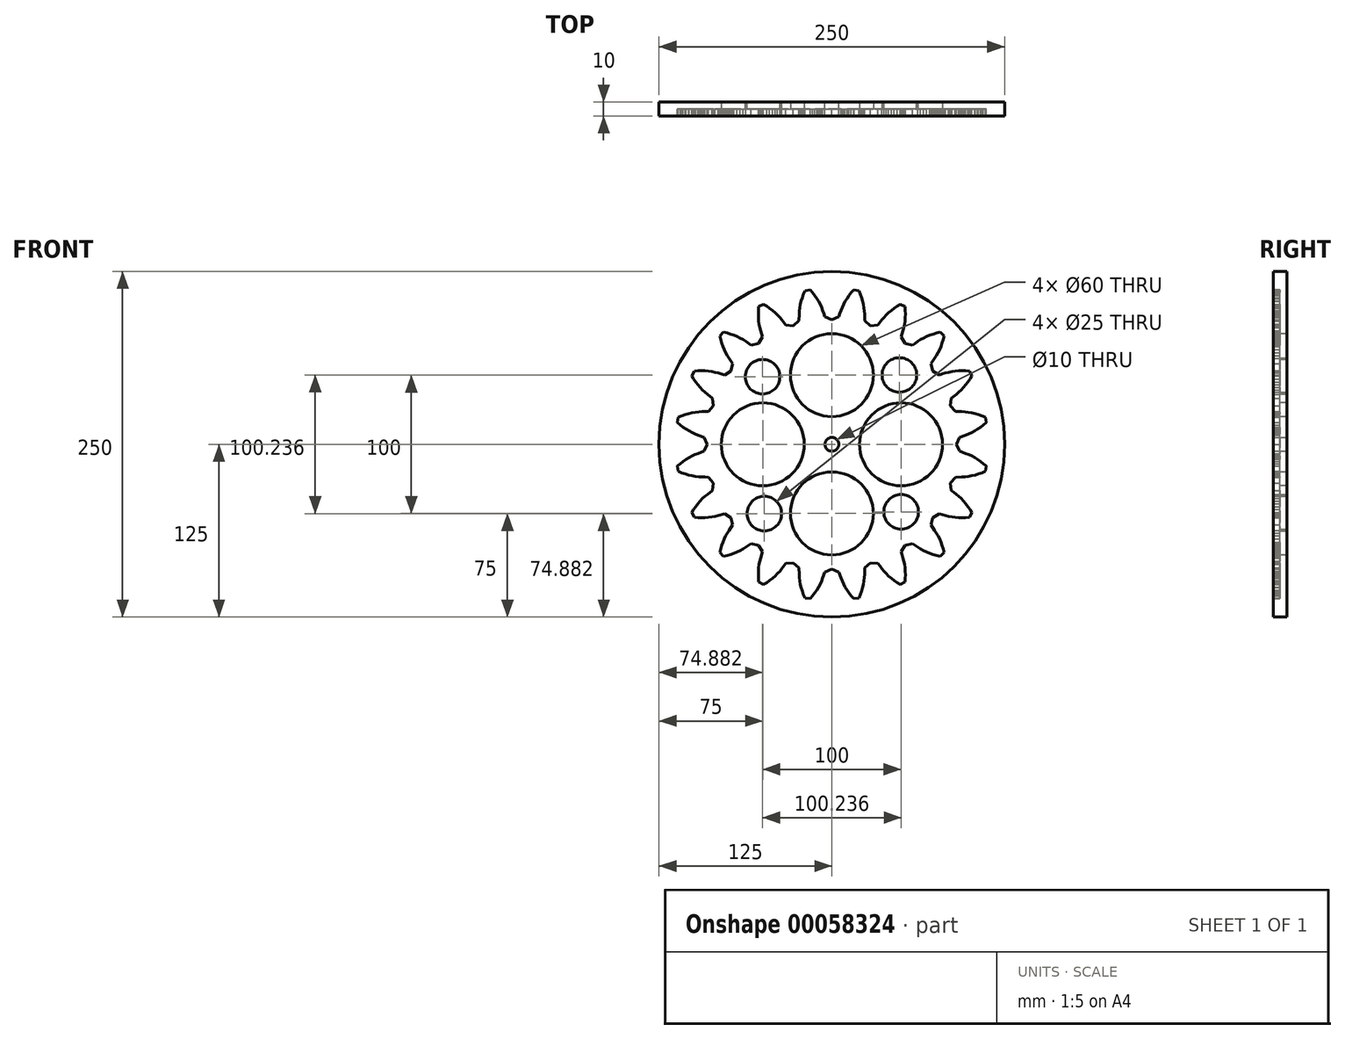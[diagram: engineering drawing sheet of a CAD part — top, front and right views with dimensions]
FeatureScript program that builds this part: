
annotation { "Feature Type Name" : "Feature", "Feature Type Description" : "" }
export const myFeature = defineFeature(function(context is Context, id is Id, definition is map)
    precondition{}
    {
        {
            var Q0;
            Q0=qCreatedBy(makeId("Front.planeOp"),FACE);
            var sketch = newSketch(context, id + "F0", { "sketchPlane" : qUnion([Q0])});
            skLineSegment(sketch, "E0", {"start": v(15.7, 111.67) * mm, "end": v(13.98, 109.62) * mm});
            skLineSegment(sketch, "E1", {"start": v(13.98, 109.62) * mm, "end": v(12.4, 107.54) * mm});
            skLineSegment(sketch, "E2", {"start": v(12.4, 107.54) * mm, "end": v(10.93, 105.44) * mm});
            skLineSegment(sketch, "E3", {"start": v(10.93, 105.44) * mm, "end": v(9.61, 103.3) * mm});
            skLineSegment(sketch, "E4", {"start": v(9.61, 103.3) * mm, "end": v(8.44, 101.14) * mm});
            skLineSegment(sketch, "E5", {"start": v(8.44, 101.14) * mm, "end": v(7.44, 98.96) * mm});
            skLineSegment(sketch, "E6", {"start": v(7.44, 98.96) * mm, "end": v(6.6, 96.75) * mm});
            skLineSegment(sketch, "E7", {"start": v(6.6, 96.75) * mm, "end": v(5.8, 94.55) * mm});
            skLineSegment(sketch, "E8", {"start": v(5.8, 94.55) * mm, "end": v(5, 92.33) * mm});
            skLineSegment(sketch, "E9", {"start": v(5, 92.33) * mm, "end": v(0, 90.21) * mm});
            skLineSegment(sketch, "E10", {"start": v(0, 90.21) * mm, "end": v(-5, 92.33) * mm});
            skLineSegment(sketch, "E11", {"start": v(-5, 92.33) * mm, "end": v(-5.8, 94.55) * mm});
            skLineSegment(sketch, "E12", {"start": v(-5.8, 94.55) * mm, "end": v(-6.6, 96.75) * mm});
            skLineSegment(sketch, "E13", {"start": v(-6.6, 96.75) * mm, "end": v(-7.44, 98.96) * mm});
            skLineSegment(sketch, "E14", {"start": v(-7.44, 98.96) * mm, "end": v(-8.44, 101.14) * mm});
            skLineSegment(sketch, "E15", {"start": v(-8.44, 101.14) * mm, "end": v(-9.61, 103.3) * mm});
            skLineSegment(sketch, "E16", {"start": v(-9.61, 103.3) * mm, "end": v(-10.93, 105.44) * mm});
            skLineSegment(sketch, "E17", {"start": v(-10.93, 105.44) * mm, "end": v(-12.4, 107.54) * mm});
            skLineSegment(sketch, "E18", {"start": v(-12.4, 107.54) * mm, "end": v(-13.98, 109.62) * mm});
            skLineSegment(sketch, "E19", {"start": v(-13.98, 109.62) * mm, "end": v(-15.7, 111.67) * mm});
            skLineSegment(sketch, "E20", {"start": v(-15.7, 111.67) * mm, "end": v(-19.57, 111.06) * mm});
            skLineSegment(sketch, "E21", {"start": v(-19.57, 111.06) * mm, "end": v(-20.58, 108.58) * mm});
            skLineSegment(sketch, "E22", {"start": v(-20.58, 108.58) * mm, "end": v(-21.45, 106.1) * mm});
            skLineSegment(sketch, "E23", {"start": v(-21.45, 106.1) * mm, "end": v(-22.18, 103.65) * mm});
            skLineSegment(sketch, "E24", {"start": v(-22.18, 103.65) * mm, "end": v(-22.78, 101.21) * mm});
            skLineSegment(sketch, "E25", {"start": v(-22.78, 101.21) * mm, "end": v(-23.22, 98.8) * mm});
            skLineSegment(sketch, "E26", {"start": v(-23.22, 98.8) * mm, "end": v(-23.5, 96.41) * mm});
            skLineSegment(sketch, "E27", {"start": v(-23.5, 96.41) * mm, "end": v(-23.62, 94.06) * mm});
            skLineSegment(sketch, "E28", {"start": v(-23.62, 94.06) * mm, "end": v(-23.7, 91.71) * mm});
            skLineSegment(sketch, "E29", {"start": v(-23.7, 91.71) * mm, "end": v(-23.78, 89.36) * mm});
            skLineSegment(sketch, "E30", {"start": v(-23.78, 89.36) * mm, "end": v(-27.88, 85.8) * mm});
            skLineSegment(sketch, "E31", {"start": v(-27.88, 85.8) * mm, "end": v(-33.28, 86.27) * mm});
            skLineSegment(sketch, "E32", {"start": v(-33.28, 86.27) * mm, "end": v(-34.73, 88.13) * mm});
            skLineSegment(sketch, "E33", {"start": v(-34.73, 88.13) * mm, "end": v(-36.18, 89.98) * mm});
            skLineSegment(sketch, "E34", {"start": v(-36.18, 89.98) * mm, "end": v(-37.65, 91.81) * mm});
            skLineSegment(sketch, "E35", {"start": v(-37.65, 91.81) * mm, "end": v(-39.28, 93.58) * mm});
            skLineSegment(sketch, "E36", {"start": v(-39.28, 93.58) * mm, "end": v(-41.06, 95.27) * mm});
            skLineSegment(sketch, "E37", {"start": v(-41.06, 95.27) * mm, "end": v(-42.98, 96.9) * mm});
            skLineSegment(sketch, "E38", {"start": v(-42.98, 96.9) * mm, "end": v(-45.02, 98.45) * mm});
            skLineSegment(sketch, "E39", {"start": v(-45.02, 98.45) * mm, "end": v(-47.18, 99.94) * mm});
            skLineSegment(sketch, "E40", {"start": v(-47.18, 99.94) * mm, "end": v(-49.44, 101.35) * mm});
            skLineSegment(sketch, "E41", {"start": v(-49.44, 101.35) * mm, "end": v(-52.93, 99.57) * mm});
            skLineSegment(sketch, "E42", {"start": v(-52.93, 99.57) * mm, "end": v(-53.12, 96.9) * mm});
            skLineSegment(sketch, "E43", {"start": v(-53.12, 96.9) * mm, "end": v(-53.19, 94.29) * mm});
            skLineSegment(sketch, "E44", {"start": v(-53.19, 94.29) * mm, "end": v(-53.13, 91.72) * mm});
            skLineSegment(sketch, "E45", {"start": v(-53.13, 91.72) * mm, "end": v(-52.94, 89.22) * mm});
            skLineSegment(sketch, "E46", {"start": v(-52.94, 89.22) * mm, "end": v(-52.62, 86.79) * mm});
            skLineSegment(sketch, "E47", {"start": v(-52.62, 86.79) * mm, "end": v(-52.15, 84.43) * mm});
            skLineSegment(sketch, "E48", {"start": v(-52.15, 84.43) * mm, "end": v(-51.53, 82.16) * mm});
            skLineSegment(sketch, "E49", {"start": v(-51.53, 82.16) * mm, "end": v(-50.88, 79.9) * mm});
            skLineSegment(sketch, "E50", {"start": v(-50.88, 79.9) * mm, "end": v(-50.23, 77.64) * mm});
            skLineSegment(sketch, "E51", {"start": v(-50.23, 77.64) * mm, "end": v(-53.03, 72.98) * mm});
            skLineSegment(sketch, "E52", {"start": v(-53.03, 72.98) * mm, "end": v(-58.31, 71.76) * mm});
            skLineSegment(sketch, "E53", {"start": v(-58.31, 71.76) * mm, "end": v(-60.27, 73.08) * mm});
            skLineSegment(sketch, "E54", {"start": v(-60.27, 73.08) * mm, "end": v(-62.21, 74.4) * mm});
            skLineSegment(sketch, "E55", {"start": v(-62.21, 74.4) * mm, "end": v(-64.18, 75.68) * mm});
            skLineSegment(sketch, "E56", {"start": v(-64.18, 75.68) * mm, "end": v(-66.28, 76.86) * mm});
            skLineSegment(sketch, "E57", {"start": v(-66.28, 76.86) * mm, "end": v(-68.5, 77.92) * mm});
            skLineSegment(sketch, "E58", {"start": v(-68.5, 77.92) * mm, "end": v(-70.82, 78.87) * mm});
            skLineSegment(sketch, "E59", {"start": v(-70.82, 78.87) * mm, "end": v(-73.24, 79.72) * mm});
            skLineSegment(sketch, "E60", {"start": v(-73.24, 79.72) * mm, "end": v(-75.75, 80.47) * mm});
            skLineSegment(sketch, "E61", {"start": v(-75.75, 80.47) * mm, "end": v(-78.34, 81.1) * mm});
            skLineSegment(sketch, "E62", {"start": v(-78.34, 81.1) * mm, "end": v(-81.1, 78.34) * mm});
            skLineSegment(sketch, "E63", {"start": v(-81.1, 78.34) * mm, "end": v(-80.47, 75.75) * mm});
            skLineSegment(sketch, "E64", {"start": v(-80.47, 75.75) * mm, "end": v(-79.72, 73.24) * mm});
            skLineSegment(sketch, "E65", {"start": v(-79.72, 73.24) * mm, "end": v(-78.87, 70.82) * mm});
            skLineSegment(sketch, "E66", {"start": v(-78.87, 70.82) * mm, "end": v(-77.92, 68.5) * mm});
            skLineSegment(sketch, "E67", {"start": v(-77.92, 68.5) * mm, "end": v(-76.86, 66.28) * mm});
            skLineSegment(sketch, "E68", {"start": v(-76.86, 66.28) * mm, "end": v(-75.68, 64.18) * mm});
            skLineSegment(sketch, "E69", {"start": v(-75.68, 64.18) * mm, "end": v(-74.4, 62.21) * mm});
            skLineSegment(sketch, "E70", {"start": v(-74.4, 62.21) * mm, "end": v(-73.08, 60.27) * mm});
            skLineSegment(sketch, "E71", {"start": v(-73.08, 60.27) * mm, "end": v(-71.76, 58.31) * mm});
            skLineSegment(sketch, "E72", {"start": v(-71.76, 58.31) * mm, "end": v(-72.98, 53.03) * mm});
            skLineSegment(sketch, "E73", {"start": v(-72.98, 53.03) * mm, "end": v(-77.64, 50.23) * mm});
            skLineSegment(sketch, "E74", {"start": v(-77.64, 50.23) * mm, "end": v(-79.9, 50.88) * mm});
            skLineSegment(sketch, "E75", {"start": v(-79.9, 50.88) * mm, "end": v(-82.16, 51.53) * mm});
            skLineSegment(sketch, "E76", {"start": v(-82.16, 51.53) * mm, "end": v(-84.43, 52.15) * mm});
            skLineSegment(sketch, "E77", {"start": v(-84.43, 52.15) * mm, "end": v(-86.79, 52.62) * mm});
            skLineSegment(sketch, "E78", {"start": v(-86.79, 52.62) * mm, "end": v(-89.22, 52.94) * mm});
            skLineSegment(sketch, "E79", {"start": v(-89.22, 52.94) * mm, "end": v(-91.72, 53.13) * mm});
            skLineSegment(sketch, "E80", {"start": v(-91.72, 53.13) * mm, "end": v(-94.29, 53.19) * mm});
            skLineSegment(sketch, "E81", {"start": v(-94.29, 53.19) * mm, "end": v(-96.9, 53.12) * mm});
            skLineSegment(sketch, "E82", {"start": v(-96.9, 53.12) * mm, "end": v(-99.57, 52.93) * mm});
            skLineSegment(sketch, "E83", {"start": v(-99.57, 52.93) * mm, "end": v(-101.35, 49.44) * mm});
            skLineSegment(sketch, "E84", {"start": v(-101.35, 49.44) * mm, "end": v(-99.94, 47.18) * mm});
            skLineSegment(sketch, "E85", {"start": v(-99.94, 47.18) * mm, "end": v(-98.45, 45.02) * mm});
            skLineSegment(sketch, "E86", {"start": v(-98.45, 45.02) * mm, "end": v(-96.9, 42.98) * mm});
            skLineSegment(sketch, "E87", {"start": v(-96.9, 42.98) * mm, "end": v(-95.27, 41.06) * mm});
            skLineSegment(sketch, "E88", {"start": v(-95.27, 41.06) * mm, "end": v(-93.58, 39.28) * mm});
            skLineSegment(sketch, "E89", {"start": v(-93.58, 39.28) * mm, "end": v(-91.81, 37.65) * mm});
            skLineSegment(sketch, "E90", {"start": v(-91.81, 37.65) * mm, "end": v(-89.98, 36.18) * mm});
            skLineSegment(sketch, "E91", {"start": v(-89.98, 36.18) * mm, "end": v(-88.13, 34.73) * mm});
            skLineSegment(sketch, "E92", {"start": v(-88.13, 34.73) * mm, "end": v(-86.27, 33.28) * mm});
            skLineSegment(sketch, "E93", {"start": v(-86.27, 33.28) * mm, "end": v(-85.8, 27.88) * mm});
            skLineSegment(sketch, "E94", {"start": v(-85.8, 27.88) * mm, "end": v(-89.36, 23.78) * mm});
            skLineSegment(sketch, "E95", {"start": v(-89.36, 23.78) * mm, "end": v(-91.71, 23.7) * mm});
            skLineSegment(sketch, "E96", {"start": v(-91.71, 23.7) * mm, "end": v(-94.06, 23.62) * mm});
            skLineSegment(sketch, "E97", {"start": v(-94.06, 23.62) * mm, "end": v(-96.41, 23.5) * mm});
            skLineSegment(sketch, "E98", {"start": v(-96.41, 23.5) * mm, "end": v(-98.8, 23.22) * mm});
            skLineSegment(sketch, "E99", {"start": v(-98.8, 23.22) * mm, "end": v(-101.21, 22.78) * mm});
            skLineSegment(sketch, "E100", {"start": v(-101.21, 22.78) * mm, "end": v(-103.65, 22.18) * mm});
            skLineSegment(sketch, "E101", {"start": v(-103.65, 22.18) * mm, "end": v(-106.1, 21.45) * mm});
            skLineSegment(sketch, "E102", {"start": v(-106.1, 21.45) * mm, "end": v(-108.58, 20.58) * mm});
            skLineSegment(sketch, "E103", {"start": v(-108.58, 20.58) * mm, "end": v(-111.06, 19.57) * mm});
            skLineSegment(sketch, "E104", {"start": v(-111.06, 19.57) * mm, "end": v(-111.67, 15.7) * mm});
            skLineSegment(sketch, "E105", {"start": v(-111.67, 15.7) * mm, "end": v(-109.62, 13.98) * mm});
            skLineSegment(sketch, "E106", {"start": v(-109.62, 13.98) * mm, "end": v(-107.54, 12.4) * mm});
            skLineSegment(sketch, "E107", {"start": v(-107.54, 12.4) * mm, "end": v(-105.44, 10.93) * mm});
            skLineSegment(sketch, "E108", {"start": v(-105.44, 10.93) * mm, "end": v(-103.3, 9.61) * mm});
            skLineSegment(sketch, "E109", {"start": v(-103.3, 9.61) * mm, "end": v(-101.14, 8.44) * mm});
            skLineSegment(sketch, "E110", {"start": v(-101.14, 8.44) * mm, "end": v(-98.96, 7.44) * mm});
            skLineSegment(sketch, "E111", {"start": v(-98.96, 7.44) * mm, "end": v(-96.75, 6.6) * mm});
            skLineSegment(sketch, "E112", {"start": v(-96.75, 6.6) * mm, "end": v(-94.55, 5.8) * mm});
            skLineSegment(sketch, "E113", {"start": v(-94.55, 5.8) * mm, "end": v(-92.33, 5) * mm});
            skLineSegment(sketch, "E114", {"start": v(-92.33, 5) * mm, "end": v(-90.21, 0) * mm});
            skLineSegment(sketch, "E115", {"start": v(-90.21, 0) * mm, "end": v(-92.33, -5) * mm});
            skLineSegment(sketch, "E116", {"start": v(-92.33, -5) * mm, "end": v(-94.55, -5.8) * mm});
            skLineSegment(sketch, "E117", {"start": v(-94.55, -5.8) * mm, "end": v(-96.75, -6.6) * mm});
            skLineSegment(sketch, "E118", {"start": v(-96.75, -6.6) * mm, "end": v(-98.96, -7.44) * mm});
            skLineSegment(sketch, "E119", {"start": v(-98.96, -7.44) * mm, "end": v(-101.14, -8.44) * mm});
            skLineSegment(sketch, "E120", {"start": v(-101.14, -8.44) * mm, "end": v(-103.3, -9.61) * mm});
            skLineSegment(sketch, "E121", {"start": v(-103.3, -9.61) * mm, "end": v(-105.44, -10.93) * mm});
            skLineSegment(sketch, "E122", {"start": v(-105.44, -10.93) * mm, "end": v(-107.54, -12.4) * mm});
            skLineSegment(sketch, "E123", {"start": v(-107.54, -12.4) * mm, "end": v(-109.62, -13.98) * mm});
            skLineSegment(sketch, "E124", {"start": v(-109.62, -13.98) * mm, "end": v(-111.67, -15.7) * mm});
            skLineSegment(sketch, "E125", {"start": v(-111.67, -15.7) * mm, "end": v(-111.06, -19.57) * mm});
            skLineSegment(sketch, "E126", {"start": v(-111.06, -19.57) * mm, "end": v(-108.58, -20.58) * mm});
            skLineSegment(sketch, "E127", {"start": v(-108.58, -20.58) * mm, "end": v(-106.1, -21.45) * mm});
            skLineSegment(sketch, "E128", {"start": v(-106.1, -21.45) * mm, "end": v(-103.65, -22.18) * mm});
            skLineSegment(sketch, "E129", {"start": v(-103.65, -22.18) * mm, "end": v(-101.21, -22.78) * mm});
            skLineSegment(sketch, "E130", {"start": v(-101.21, -22.78) * mm, "end": v(-98.8, -23.22) * mm});
            skLineSegment(sketch, "E131", {"start": v(-98.8, -23.22) * mm, "end": v(-96.41, -23.5) * mm});
            skLineSegment(sketch, "E132", {"start": v(-96.41, -23.5) * mm, "end": v(-94.06, -23.62) * mm});
            skLineSegment(sketch, "E133", {"start": v(-94.06, -23.62) * mm, "end": v(-91.71, -23.7) * mm});
            skLineSegment(sketch, "E134", {"start": v(-91.71, -23.7) * mm, "end": v(-89.36, -23.78) * mm});
            skLineSegment(sketch, "E135", {"start": v(-89.36, -23.78) * mm, "end": v(-85.8, -27.88) * mm});
            skLineSegment(sketch, "E136", {"start": v(-85.8, -27.88) * mm, "end": v(-86.27, -33.28) * mm});
            skLineSegment(sketch, "E137", {"start": v(-86.27, -33.28) * mm, "end": v(-88.13, -34.73) * mm});
            skLineSegment(sketch, "E138", {"start": v(-88.13, -34.73) * mm, "end": v(-89.98, -36.18) * mm});
            skLineSegment(sketch, "E139", {"start": v(-89.98, -36.18) * mm, "end": v(-91.81, -37.65) * mm});
            skLineSegment(sketch, "E140", {"start": v(-91.81, -37.65) * mm, "end": v(-93.58, -39.28) * mm});
            skLineSegment(sketch, "E141", {"start": v(-93.58, -39.28) * mm, "end": v(-95.27, -41.06) * mm});
            skLineSegment(sketch, "E142", {"start": v(-95.27, -41.06) * mm, "end": v(-96.9, -42.98) * mm});
            skLineSegment(sketch, "E143", {"start": v(-96.9, -42.98) * mm, "end": v(-98.45, -45.02) * mm});
            skLineSegment(sketch, "E144", {"start": v(-98.45, -45.02) * mm, "end": v(-99.94, -47.18) * mm});
            skLineSegment(sketch, "E145", {"start": v(-99.94, -47.18) * mm, "end": v(-101.35, -49.44) * mm});
            skLineSegment(sketch, "E146", {"start": v(-101.35, -49.44) * mm, "end": v(-99.57, -52.93) * mm});
            skLineSegment(sketch, "E147", {"start": v(-99.57, -52.93) * mm, "end": v(-96.9, -53.12) * mm});
            skLineSegment(sketch, "E148", {"start": v(-96.9, -53.12) * mm, "end": v(-94.29, -53.19) * mm});
            skLineSegment(sketch, "E149", {"start": v(-94.29, -53.19) * mm, "end": v(-91.72, -53.13) * mm});
            skLineSegment(sketch, "E150", {"start": v(-91.72, -53.13) * mm, "end": v(-89.22, -52.94) * mm});
            skLineSegment(sketch, "E151", {"start": v(-89.22, -52.94) * mm, "end": v(-86.79, -52.62) * mm});
            skLineSegment(sketch, "E152", {"start": v(-86.79, -52.62) * mm, "end": v(-84.43, -52.15) * mm});
            skLineSegment(sketch, "E153", {"start": v(-84.43, -52.15) * mm, "end": v(-82.16, -51.53) * mm});
            skLineSegment(sketch, "E154", {"start": v(-82.16, -51.53) * mm, "end": v(-79.9, -50.88) * mm});
            skLineSegment(sketch, "E155", {"start": v(-79.9, -50.88) * mm, "end": v(-77.64, -50.23) * mm});
            skLineSegment(sketch, "E156", {"start": v(-77.64, -50.23) * mm, "end": v(-72.98, -53.03) * mm});
            skLineSegment(sketch, "E157", {"start": v(-72.98, -53.03) * mm, "end": v(-71.76, -58.31) * mm});
            skLineSegment(sketch, "E158", {"start": v(-71.76, -58.31) * mm, "end": v(-73.08, -60.27) * mm});
            skLineSegment(sketch, "E159", {"start": v(-73.08, -60.27) * mm, "end": v(-74.4, -62.21) * mm});
            skLineSegment(sketch, "E160", {"start": v(-74.4, -62.21) * mm, "end": v(-75.68, -64.18) * mm});
            skLineSegment(sketch, "E161", {"start": v(-75.68, -64.18) * mm, "end": v(-76.86, -66.28) * mm});
            skLineSegment(sketch, "E162", {"start": v(-76.86, -66.28) * mm, "end": v(-77.92, -68.5) * mm});
            skLineSegment(sketch, "E163", {"start": v(-77.92, -68.5) * mm, "end": v(-78.87, -70.82) * mm});
            skLineSegment(sketch, "E164", {"start": v(-78.87, -70.82) * mm, "end": v(-79.72, -73.24) * mm});
            skLineSegment(sketch, "E165", {"start": v(-79.72, -73.24) * mm, "end": v(-80.47, -75.75) * mm});
            skLineSegment(sketch, "E166", {"start": v(-80.47, -75.75) * mm, "end": v(-81.1, -78.34) * mm});
            skLineSegment(sketch, "E167", {"start": v(-81.1, -78.34) * mm, "end": v(-78.34, -81.1) * mm});
            skLineSegment(sketch, "E168", {"start": v(-78.34, -81.1) * mm, "end": v(-75.75, -80.47) * mm});
            skLineSegment(sketch, "E169", {"start": v(-75.75, -80.47) * mm, "end": v(-73.24, -79.72) * mm});
            skLineSegment(sketch, "E170", {"start": v(-73.24, -79.72) * mm, "end": v(-70.82, -78.87) * mm});
            skLineSegment(sketch, "E171", {"start": v(-70.82, -78.87) * mm, "end": v(-68.5, -77.92) * mm});
            skLineSegment(sketch, "E172", {"start": v(-68.5, -77.92) * mm, "end": v(-66.28, -76.86) * mm});
            skLineSegment(sketch, "E173", {"start": v(-66.28, -76.86) * mm, "end": v(-64.18, -75.68) * mm});
            skLineSegment(sketch, "E174", {"start": v(-64.18, -75.68) * mm, "end": v(-62.21, -74.4) * mm});
            skLineSegment(sketch, "E175", {"start": v(-62.21, -74.4) * mm, "end": v(-60.27, -73.08) * mm});
            skLineSegment(sketch, "E176", {"start": v(-60.27, -73.08) * mm, "end": v(-58.31, -71.76) * mm});
            skLineSegment(sketch, "E177", {"start": v(-58.31, -71.76) * mm, "end": v(-53.03, -72.98) * mm});
            skLineSegment(sketch, "E178", {"start": v(-53.03, -72.98) * mm, "end": v(-50.23, -77.64) * mm});
            skLineSegment(sketch, "E179", {"start": v(-50.23, -77.64) * mm, "end": v(-50.88, -79.9) * mm});
            skLineSegment(sketch, "E180", {"start": v(-50.88, -79.9) * mm, "end": v(-51.53, -82.16) * mm});
            skLineSegment(sketch, "E181", {"start": v(-51.53, -82.16) * mm, "end": v(-52.15, -84.43) * mm});
            skLineSegment(sketch, "E182", {"start": v(-52.15, -84.43) * mm, "end": v(-52.62, -86.79) * mm});
            skLineSegment(sketch, "E183", {"start": v(-52.62, -86.79) * mm, "end": v(-52.94, -89.22) * mm});
            skLineSegment(sketch, "E184", {"start": v(-52.94, -89.22) * mm, "end": v(-53.13, -91.72) * mm});
            skLineSegment(sketch, "E185", {"start": v(-53.13, -91.72) * mm, "end": v(-53.19, -94.29) * mm});
            skLineSegment(sketch, "E186", {"start": v(-53.19, -94.29) * mm, "end": v(-53.12, -96.9) * mm});
            skLineSegment(sketch, "E187", {"start": v(-53.12, -96.9) * mm, "end": v(-52.93, -99.57) * mm});
            skLineSegment(sketch, "E188", {"start": v(-52.93, -99.57) * mm, "end": v(-49.44, -101.35) * mm});
            skLineSegment(sketch, "E189", {"start": v(-49.44, -101.35) * mm, "end": v(-47.18, -99.94) * mm});
            skLineSegment(sketch, "E190", {"start": v(-47.18, -99.94) * mm, "end": v(-45.02, -98.45) * mm});
            skLineSegment(sketch, "E191", {"start": v(-45.02, -98.45) * mm, "end": v(-42.98, -96.9) * mm});
            skLineSegment(sketch, "E192", {"start": v(-42.98, -96.9) * mm, "end": v(-41.06, -95.27) * mm});
            skLineSegment(sketch, "E193", {"start": v(-41.06, -95.27) * mm, "end": v(-39.28, -93.58) * mm});
            skLineSegment(sketch, "E194", {"start": v(-39.28, -93.58) * mm, "end": v(-37.65, -91.81) * mm});
            skLineSegment(sketch, "E195", {"start": v(-37.65, -91.81) * mm, "end": v(-36.18, -89.98) * mm});
            skLineSegment(sketch, "E196", {"start": v(-36.18, -89.98) * mm, "end": v(-34.73, -88.13) * mm});
            skLineSegment(sketch, "E197", {"start": v(-34.73, -88.13) * mm, "end": v(-33.28, -86.27) * mm});
            skLineSegment(sketch, "E198", {"start": v(-33.28, -86.27) * mm, "end": v(-27.88, -85.8) * mm});
            skLineSegment(sketch, "E199", {"start": v(-27.88, -85.8) * mm, "end": v(-23.78, -89.36) * mm});
            skLineSegment(sketch, "E200", {"start": v(-23.78, -89.36) * mm, "end": v(-23.7, -91.71) * mm});
            skLineSegment(sketch, "E201", {"start": v(-23.7, -91.71) * mm, "end": v(-23.62, -94.06) * mm});
            skLineSegment(sketch, "E202", {"start": v(-23.62, -94.06) * mm, "end": v(-23.5, -96.41) * mm});
            skLineSegment(sketch, "E203", {"start": v(-23.5, -96.41) * mm, "end": v(-23.22, -98.8) * mm});
            skLineSegment(sketch, "E204", {"start": v(-23.22, -98.8) * mm, "end": v(-22.78, -101.21) * mm});
            skLineSegment(sketch, "E205", {"start": v(-22.78, -101.21) * mm, "end": v(-22.18, -103.65) * mm});
            skLineSegment(sketch, "E206", {"start": v(-22.18, -103.65) * mm, "end": v(-21.45, -106.1) * mm});
            skLineSegment(sketch, "E207", {"start": v(-21.45, -106.1) * mm, "end": v(-20.58, -108.58) * mm});
            skLineSegment(sketch, "E208", {"start": v(-20.58, -108.58) * mm, "end": v(-19.57, -111.06) * mm});
            skLineSegment(sketch, "E209", {"start": v(-19.57, -111.06) * mm, "end": v(-15.7, -111.67) * mm});
            skLineSegment(sketch, "E210", {"start": v(-15.7, -111.67) * mm, "end": v(-13.98, -109.62) * mm});
            skLineSegment(sketch, "E211", {"start": v(-13.98, -109.62) * mm, "end": v(-12.4, -107.54) * mm});
            skLineSegment(sketch, "E212", {"start": v(-12.4, -107.54) * mm, "end": v(-10.93, -105.44) * mm});
            skLineSegment(sketch, "E213", {"start": v(-10.93, -105.44) * mm, "end": v(-9.61, -103.3) * mm});
            skLineSegment(sketch, "E214", {"start": v(-9.61, -103.3) * mm, "end": v(-8.44, -101.14) * mm});
            skLineSegment(sketch, "E215", {"start": v(-8.44, -101.14) * mm, "end": v(-7.44, -98.96) * mm});
            skLineSegment(sketch, "E216", {"start": v(-7.44, -98.96) * mm, "end": v(-6.6, -96.75) * mm});
            skLineSegment(sketch, "E217", {"start": v(-6.6, -96.75) * mm, "end": v(-5.8, -94.55) * mm});
            skLineSegment(sketch, "E218", {"start": v(-5.8, -94.55) * mm, "end": v(-5, -92.33) * mm});
            skLineSegment(sketch, "E219", {"start": v(-5, -92.33) * mm, "end": v(0, -90.21) * mm});
            skLineSegment(sketch, "E220", {"start": v(0, -90.21) * mm, "end": v(5, -92.33) * mm});
            skLineSegment(sketch, "E221", {"start": v(5, -92.33) * mm, "end": v(5.8, -94.55) * mm});
            skLineSegment(sketch, "E222", {"start": v(5.8, -94.55) * mm, "end": v(6.6, -96.75) * mm});
            skLineSegment(sketch, "E223", {"start": v(6.6, -96.75) * mm, "end": v(7.44, -98.96) * mm});
            skLineSegment(sketch, "E224", {"start": v(7.44, -98.96) * mm, "end": v(8.44, -101.14) * mm});
            skLineSegment(sketch, "E225", {"start": v(8.44, -101.14) * mm, "end": v(9.61, -103.3) * mm});
            skLineSegment(sketch, "E226", {"start": v(9.61, -103.3) * mm, "end": v(10.93, -105.44) * mm});
            skLineSegment(sketch, "E227", {"start": v(10.93, -105.44) * mm, "end": v(12.4, -107.54) * mm});
            skLineSegment(sketch, "E228", {"start": v(12.4, -107.54) * mm, "end": v(13.98, -109.62) * mm});
            skLineSegment(sketch, "E229", {"start": v(13.98, -109.62) * mm, "end": v(15.7, -111.67) * mm});
            skLineSegment(sketch, "E230", {"start": v(15.7, -111.67) * mm, "end": v(19.57, -111.06) * mm});
            skLineSegment(sketch, "E231", {"start": v(19.57, -111.06) * mm, "end": v(20.58, -108.58) * mm});
            skLineSegment(sketch, "E232", {"start": v(20.58, -108.58) * mm, "end": v(21.45, -106.1) * mm});
            skLineSegment(sketch, "E233", {"start": v(21.45, -106.1) * mm, "end": v(22.18, -103.65) * mm});
            skLineSegment(sketch, "E234", {"start": v(22.18, -103.65) * mm, "end": v(22.78, -101.21) * mm});
            skLineSegment(sketch, "E235", {"start": v(22.78, -101.21) * mm, "end": v(23.22, -98.8) * mm});
            skLineSegment(sketch, "E236", {"start": v(23.22, -98.8) * mm, "end": v(23.5, -96.41) * mm});
            skLineSegment(sketch, "E237", {"start": v(23.5, -96.41) * mm, "end": v(23.62, -94.06) * mm});
            skLineSegment(sketch, "E238", {"start": v(23.62, -94.06) * mm, "end": v(23.7, -91.71) * mm});
            skLineSegment(sketch, "E239", {"start": v(23.7, -91.71) * mm, "end": v(23.78, -89.36) * mm});
            skLineSegment(sketch, "E240", {"start": v(23.78, -89.36) * mm, "end": v(27.88, -85.8) * mm});
            skLineSegment(sketch, "E241", {"start": v(27.88, -85.8) * mm, "end": v(33.28, -86.27) * mm});
            skLineSegment(sketch, "E242", {"start": v(33.28, -86.27) * mm, "end": v(34.73, -88.13) * mm});
            skLineSegment(sketch, "E243", {"start": v(34.73, -88.13) * mm, "end": v(36.18, -89.98) * mm});
            skLineSegment(sketch, "E244", {"start": v(36.18, -89.98) * mm, "end": v(37.65, -91.81) * mm});
            skLineSegment(sketch, "E245", {"start": v(37.65, -91.81) * mm, "end": v(39.28, -93.58) * mm});
            skLineSegment(sketch, "E246", {"start": v(39.28, -93.58) * mm, "end": v(41.06, -95.27) * mm});
            skLineSegment(sketch, "E247", {"start": v(41.06, -95.27) * mm, "end": v(42.98, -96.9) * mm});
            skLineSegment(sketch, "E248", {"start": v(42.98, -96.9) * mm, "end": v(45.02, -98.45) * mm});
            skLineSegment(sketch, "E249", {"start": v(45.02, -98.45) * mm, "end": v(47.18, -99.94) * mm});
            skLineSegment(sketch, "E250", {"start": v(47.18, -99.94) * mm, "end": v(49.44, -101.35) * mm});
            skLineSegment(sketch, "E251", {"start": v(49.44, -101.35) * mm, "end": v(52.93, -99.57) * mm});
            skLineSegment(sketch, "E252", {"start": v(52.93, -99.57) * mm, "end": v(53.12, -96.9) * mm});
            skLineSegment(sketch, "E253", {"start": v(53.12, -96.9) * mm, "end": v(53.19, -94.29) * mm});
            skLineSegment(sketch, "E254", {"start": v(53.19, -94.29) * mm, "end": v(53.13, -91.72) * mm});
            skLineSegment(sketch, "E255", {"start": v(53.13, -91.72) * mm, "end": v(52.94, -89.22) * mm});
            skLineSegment(sketch, "E256", {"start": v(52.94, -89.22) * mm, "end": v(52.62, -86.79) * mm});
            skLineSegment(sketch, "E257", {"start": v(52.62, -86.79) * mm, "end": v(52.15, -84.43) * mm});
            skLineSegment(sketch, "E258", {"start": v(52.15, -84.43) * mm, "end": v(51.53, -82.16) * mm});
            skLineSegment(sketch, "E259", {"start": v(51.53, -82.16) * mm, "end": v(50.88, -79.9) * mm});
            skLineSegment(sketch, "E260", {"start": v(50.88, -79.9) * mm, "end": v(50.23, -77.64) * mm});
            skLineSegment(sketch, "E261", {"start": v(50.23, -77.64) * mm, "end": v(53.03, -72.98) * mm});
            skLineSegment(sketch, "E262", {"start": v(53.03, -72.98) * mm, "end": v(58.31, -71.76) * mm});
            skLineSegment(sketch, "E263", {"start": v(58.31, -71.76) * mm, "end": v(60.27, -73.08) * mm});
            skLineSegment(sketch, "E264", {"start": v(60.27, -73.08) * mm, "end": v(62.21, -74.4) * mm});
            skLineSegment(sketch, "E265", {"start": v(62.21, -74.4) * mm, "end": v(64.18, -75.68) * mm});
            skLineSegment(sketch, "E266", {"start": v(64.18, -75.68) * mm, "end": v(66.28, -76.86) * mm});
            skLineSegment(sketch, "E267", {"start": v(66.28, -76.86) * mm, "end": v(68.5, -77.92) * mm});
            skLineSegment(sketch, "E268", {"start": v(68.5, -77.92) * mm, "end": v(70.82, -78.87) * mm});
            skLineSegment(sketch, "E269", {"start": v(70.82, -78.87) * mm, "end": v(73.24, -79.72) * mm});
            skLineSegment(sketch, "E270", {"start": v(73.24, -79.72) * mm, "end": v(75.75, -80.47) * mm});
            skLineSegment(sketch, "E271", {"start": v(75.75, -80.47) * mm, "end": v(78.34, -81.1) * mm});
            skLineSegment(sketch, "E272", {"start": v(78.34, -81.1) * mm, "end": v(81.1, -78.34) * mm});
            skLineSegment(sketch, "E273", {"start": v(81.1, -78.34) * mm, "end": v(80.47, -75.75) * mm});
            skLineSegment(sketch, "E274", {"start": v(80.47, -75.75) * mm, "end": v(79.72, -73.24) * mm});
            skLineSegment(sketch, "E275", {"start": v(79.72, -73.24) * mm, "end": v(78.87, -70.82) * mm});
            skLineSegment(sketch, "E276", {"start": v(78.87, -70.82) * mm, "end": v(77.92, -68.5) * mm});
            skLineSegment(sketch, "E277", {"start": v(77.92, -68.5) * mm, "end": v(76.86, -66.28) * mm});
            skLineSegment(sketch, "E278", {"start": v(76.86, -66.28) * mm, "end": v(75.68, -64.18) * mm});
            skLineSegment(sketch, "E279", {"start": v(75.68, -64.18) * mm, "end": v(74.4, -62.21) * mm});
            skLineSegment(sketch, "E280", {"start": v(74.4, -62.21) * mm, "end": v(73.08, -60.27) * mm});
            skLineSegment(sketch, "E281", {"start": v(73.08, -60.27) * mm, "end": v(71.76, -58.31) * mm});
            skLineSegment(sketch, "E282", {"start": v(71.76, -58.31) * mm, "end": v(72.98, -53.03) * mm});
            skLineSegment(sketch, "E283", {"start": v(72.98, -53.03) * mm, "end": v(77.64, -50.23) * mm});
            skLineSegment(sketch, "E284", {"start": v(77.64, -50.23) * mm, "end": v(79.9, -50.88) * mm});
            skLineSegment(sketch, "E285", {"start": v(79.9, -50.88) * mm, "end": v(82.16, -51.53) * mm});
            skLineSegment(sketch, "E286", {"start": v(82.16, -51.53) * mm, "end": v(84.43, -52.15) * mm});
            skLineSegment(sketch, "E287", {"start": v(84.43, -52.15) * mm, "end": v(86.79, -52.62) * mm});
            skLineSegment(sketch, "E288", {"start": v(86.79, -52.62) * mm, "end": v(89.22, -52.94) * mm});
            skLineSegment(sketch, "E289", {"start": v(89.22, -52.94) * mm, "end": v(91.72, -53.13) * mm});
            skLineSegment(sketch, "E290", {"start": v(91.72, -53.13) * mm, "end": v(94.29, -53.19) * mm});
            skLineSegment(sketch, "E291", {"start": v(94.29, -53.19) * mm, "end": v(96.9, -53.12) * mm});
            skLineSegment(sketch, "E292", {"start": v(96.9, -53.12) * mm, "end": v(99.57, -52.93) * mm});
            skLineSegment(sketch, "E293", {"start": v(99.57, -52.93) * mm, "end": v(101.35, -49.44) * mm});
            skLineSegment(sketch, "E294", {"start": v(101.35, -49.44) * mm, "end": v(99.94, -47.18) * mm});
            skLineSegment(sketch, "E295", {"start": v(99.94, -47.18) * mm, "end": v(98.45, -45.02) * mm});
            skLineSegment(sketch, "E296", {"start": v(98.45, -45.02) * mm, "end": v(96.9, -42.98) * mm});
            skLineSegment(sketch, "E297", {"start": v(96.9, -42.98) * mm, "end": v(95.27, -41.06) * mm});
            skLineSegment(sketch, "E298", {"start": v(95.27, -41.06) * mm, "end": v(93.58, -39.28) * mm});
            skLineSegment(sketch, "E299", {"start": v(93.58, -39.28) * mm, "end": v(91.81, -37.65) * mm});
            skLineSegment(sketch, "E300", {"start": v(91.81, -37.65) * mm, "end": v(89.98, -36.18) * mm});
            skLineSegment(sketch, "E301", {"start": v(89.98, -36.18) * mm, "end": v(88.13, -34.73) * mm});
            skLineSegment(sketch, "E302", {"start": v(88.13, -34.73) * mm, "end": v(86.27, -33.28) * mm});
            skLineSegment(sketch, "E303", {"start": v(86.27, -33.28) * mm, "end": v(85.8, -27.88) * mm});
            skLineSegment(sketch, "E304", {"start": v(85.8, -27.88) * mm, "end": v(89.36, -23.78) * mm});
            skLineSegment(sketch, "E305", {"start": v(89.36, -23.78) * mm, "end": v(91.71, -23.7) * mm});
            skLineSegment(sketch, "E306", {"start": v(91.71, -23.7) * mm, "end": v(94.06, -23.62) * mm});
            skLineSegment(sketch, "E307", {"start": v(94.06, -23.62) * mm, "end": v(96.41, -23.5) * mm});
            skLineSegment(sketch, "E308", {"start": v(96.41, -23.5) * mm, "end": v(98.8, -23.22) * mm});
            skLineSegment(sketch, "E309", {"start": v(98.8, -23.22) * mm, "end": v(101.21, -22.78) * mm});
            skLineSegment(sketch, "E310", {"start": v(101.21, -22.78) * mm, "end": v(103.65, -22.18) * mm});
            skLineSegment(sketch, "E311", {"start": v(103.65, -22.18) * mm, "end": v(106.1, -21.45) * mm});
            skLineSegment(sketch, "E312", {"start": v(106.1, -21.45) * mm, "end": v(108.58, -20.58) * mm});
            skLineSegment(sketch, "E313", {"start": v(108.58, -20.58) * mm, "end": v(111.06, -19.57) * mm});
            skLineSegment(sketch, "E314", {"start": v(111.06, -19.57) * mm, "end": v(111.67, -15.7) * mm});
            skLineSegment(sketch, "E315", {"start": v(111.67, -15.7) * mm, "end": v(109.62, -13.98) * mm});
            skLineSegment(sketch, "E316", {"start": v(109.62, -13.98) * mm, "end": v(107.54, -12.4) * mm});
            skLineSegment(sketch, "E317", {"start": v(107.54, -12.4) * mm, "end": v(105.44, -10.93) * mm});
            skLineSegment(sketch, "E318", {"start": v(105.44, -10.93) * mm, "end": v(103.3, -9.61) * mm});
            skLineSegment(sketch, "E319", {"start": v(103.3, -9.61) * mm, "end": v(101.14, -8.44) * mm});
            skLineSegment(sketch, "E320", {"start": v(101.14, -8.44) * mm, "end": v(98.96, -7.44) * mm});
            skLineSegment(sketch, "E321", {"start": v(98.96, -7.44) * mm, "end": v(96.75, -6.6) * mm});
            skLineSegment(sketch, "E322", {"start": v(96.75, -6.6) * mm, "end": v(94.55, -5.8) * mm});
            skLineSegment(sketch, "E323", {"start": v(94.55, -5.8) * mm, "end": v(92.33, -5) * mm});
            skLineSegment(sketch, "E324", {"start": v(92.33, -5) * mm, "end": v(90.21, 0) * mm});
            skLineSegment(sketch, "E325", {"start": v(90.21, 0) * mm, "end": v(92.33, 5) * mm});
            skLineSegment(sketch, "E326", {"start": v(92.33, 5) * mm, "end": v(94.55, 5.8) * mm});
            skLineSegment(sketch, "E327", {"start": v(94.55, 5.8) * mm, "end": v(96.75, 6.6) * mm});
            skLineSegment(sketch, "E328", {"start": v(96.75, 6.6) * mm, "end": v(98.96, 7.44) * mm});
            skLineSegment(sketch, "E329", {"start": v(98.96, 7.44) * mm, "end": v(101.14, 8.44) * mm});
            skLineSegment(sketch, "E330", {"start": v(101.14, 8.44) * mm, "end": v(103.3, 9.61) * mm});
            skLineSegment(sketch, "E331", {"start": v(103.3, 9.61) * mm, "end": v(105.44, 10.93) * mm});
            skLineSegment(sketch, "E332", {"start": v(105.44, 10.93) * mm, "end": v(107.54, 12.4) * mm});
            skLineSegment(sketch, "E333", {"start": v(107.54, 12.4) * mm, "end": v(109.62, 13.98) * mm});
            skLineSegment(sketch, "E334", {"start": v(109.62, 13.98) * mm, "end": v(111.67, 15.7) * mm});
            skLineSegment(sketch, "E335", {"start": v(111.67, 15.7) * mm, "end": v(111.06, 19.57) * mm});
            skLineSegment(sketch, "E336", {"start": v(111.06, 19.57) * mm, "end": v(108.58, 20.58) * mm});
            skLineSegment(sketch, "E337", {"start": v(108.58, 20.58) * mm, "end": v(106.1, 21.45) * mm});
            skLineSegment(sketch, "E338", {"start": v(106.1, 21.45) * mm, "end": v(103.65, 22.18) * mm});
            skLineSegment(sketch, "E339", {"start": v(103.65, 22.18) * mm, "end": v(101.21, 22.78) * mm});
            skLineSegment(sketch, "E340", {"start": v(101.21, 22.78) * mm, "end": v(98.8, 23.22) * mm});
            skLineSegment(sketch, "E341", {"start": v(98.8, 23.22) * mm, "end": v(96.41, 23.5) * mm});
            skLineSegment(sketch, "E342", {"start": v(96.41, 23.5) * mm, "end": v(94.06, 23.62) * mm});
            skLineSegment(sketch, "E343", {"start": v(94.06, 23.62) * mm, "end": v(91.71, 23.7) * mm});
            skLineSegment(sketch, "E344", {"start": v(91.71, 23.7) * mm, "end": v(89.36, 23.78) * mm});
            skLineSegment(sketch, "E345", {"start": v(89.36, 23.78) * mm, "end": v(85.8, 27.88) * mm});
            skLineSegment(sketch, "E346", {"start": v(85.8, 27.88) * mm, "end": v(86.27, 33.28) * mm});
            skLineSegment(sketch, "E347", {"start": v(86.27, 33.28) * mm, "end": v(88.13, 34.73) * mm});
            skLineSegment(sketch, "E348", {"start": v(88.13, 34.73) * mm, "end": v(89.98, 36.18) * mm});
            skLineSegment(sketch, "E349", {"start": v(89.98, 36.18) * mm, "end": v(91.81, 37.65) * mm});
            skLineSegment(sketch, "E350", {"start": v(91.81, 37.65) * mm, "end": v(93.58, 39.28) * mm});
            skLineSegment(sketch, "E351", {"start": v(93.58, 39.28) * mm, "end": v(95.27, 41.06) * mm});
            skLineSegment(sketch, "E352", {"start": v(95.27, 41.06) * mm, "end": v(96.9, 42.98) * mm});
            skLineSegment(sketch, "E353", {"start": v(96.9, 42.98) * mm, "end": v(98.45, 45.02) * mm});
            skLineSegment(sketch, "E354", {"start": v(98.45, 45.02) * mm, "end": v(99.94, 47.18) * mm});
            skLineSegment(sketch, "E355", {"start": v(99.94, 47.18) * mm, "end": v(101.35, 49.44) * mm});
            skLineSegment(sketch, "E356", {"start": v(101.35, 49.44) * mm, "end": v(99.57, 52.93) * mm});
            skLineSegment(sketch, "E357", {"start": v(99.57, 52.93) * mm, "end": v(96.9, 53.12) * mm});
            skLineSegment(sketch, "E358", {"start": v(96.9, 53.12) * mm, "end": v(94.29, 53.19) * mm});
            skLineSegment(sketch, "E359", {"start": v(94.29, 53.19) * mm, "end": v(91.72, 53.13) * mm});
            skLineSegment(sketch, "E360", {"start": v(91.72, 53.13) * mm, "end": v(89.22, 52.94) * mm});
            skLineSegment(sketch, "E361", {"start": v(89.22, 52.94) * mm, "end": v(86.79, 52.62) * mm});
            skLineSegment(sketch, "E362", {"start": v(86.79, 52.62) * mm, "end": v(84.43, 52.15) * mm});
            skLineSegment(sketch, "E363", {"start": v(84.43, 52.15) * mm, "end": v(82.16, 51.53) * mm});
            skLineSegment(sketch, "E364", {"start": v(82.16, 51.53) * mm, "end": v(79.9, 50.88) * mm});
            skLineSegment(sketch, "E365", {"start": v(79.9, 50.88) * mm, "end": v(77.64, 50.23) * mm});
            skLineSegment(sketch, "E366", {"start": v(77.64, 50.23) * mm, "end": v(72.98, 53.03) * mm});
            skLineSegment(sketch, "E367", {"start": v(72.98, 53.03) * mm, "end": v(71.76, 58.31) * mm});
            skLineSegment(sketch, "E368", {"start": v(71.76, 58.31) * mm, "end": v(73.08, 60.27) * mm});
            skLineSegment(sketch, "E369", {"start": v(73.08, 60.27) * mm, "end": v(74.4, 62.21) * mm});
            skLineSegment(sketch, "E370", {"start": v(74.4, 62.21) * mm, "end": v(75.68, 64.18) * mm});
            skLineSegment(sketch, "E371", {"start": v(75.68, 64.18) * mm, "end": v(76.86, 66.28) * mm});
            skLineSegment(sketch, "E372", {"start": v(76.86, 66.28) * mm, "end": v(77.92, 68.5) * mm});
            skLineSegment(sketch, "E373", {"start": v(77.92, 68.5) * mm, "end": v(78.87, 70.82) * mm});
            skLineSegment(sketch, "E374", {"start": v(78.87, 70.82) * mm, "end": v(79.72, 73.24) * mm});
            skLineSegment(sketch, "E375", {"start": v(79.72, 73.24) * mm, "end": v(80.47, 75.75) * mm});
            skLineSegment(sketch, "E376", {"start": v(80.47, 75.75) * mm, "end": v(81.1, 78.34) * mm});
            skLineSegment(sketch, "E377", {"start": v(81.1, 78.34) * mm, "end": v(78.34, 81.1) * mm});
            skLineSegment(sketch, "E378", {"start": v(78.34, 81.1) * mm, "end": v(75.75, 80.47) * mm});
            skLineSegment(sketch, "E379", {"start": v(75.75, 80.47) * mm, "end": v(73.24, 79.72) * mm});
            skLineSegment(sketch, "E380", {"start": v(73.24, 79.72) * mm, "end": v(70.82, 78.87) * mm});
            skLineSegment(sketch, "E381", {"start": v(70.82, 78.87) * mm, "end": v(68.5, 77.92) * mm});
            skLineSegment(sketch, "E382", {"start": v(68.5, 77.92) * mm, "end": v(66.28, 76.86) * mm});
            skLineSegment(sketch, "E383", {"start": v(66.28, 76.86) * mm, "end": v(64.18, 75.68) * mm});
            skLineSegment(sketch, "E384", {"start": v(64.18, 75.68) * mm, "end": v(62.21, 74.4) * mm});
            skLineSegment(sketch, "E385", {"start": v(62.21, 74.4) * mm, "end": v(60.27, 73.08) * mm});
            skLineSegment(sketch, "E386", {"start": v(60.27, 73.08) * mm, "end": v(58.31, 71.76) * mm});
            skLineSegment(sketch, "E387", {"start": v(58.31, 71.76) * mm, "end": v(53.03, 72.98) * mm});
            skLineSegment(sketch, "E388", {"start": v(53.03, 72.98) * mm, "end": v(50.23, 77.64) * mm});
            skLineSegment(sketch, "E389", {"start": v(50.23, 77.64) * mm, "end": v(50.88, 79.9) * mm});
            skLineSegment(sketch, "E390", {"start": v(50.88, 79.9) * mm, "end": v(51.53, 82.16) * mm});
            skLineSegment(sketch, "E391", {"start": v(51.53, 82.16) * mm, "end": v(52.15, 84.43) * mm});
            skLineSegment(sketch, "E392", {"start": v(52.15, 84.43) * mm, "end": v(52.62, 86.79) * mm});
            skLineSegment(sketch, "E393", {"start": v(52.62, 86.79) * mm, "end": v(52.94, 89.22) * mm});
            skLineSegment(sketch, "E394", {"start": v(52.94, 89.22) * mm, "end": v(53.13, 91.72) * mm});
            skLineSegment(sketch, "E395", {"start": v(53.13, 91.72) * mm, "end": v(53.19, 94.29) * mm});
            skLineSegment(sketch, "E396", {"start": v(53.19, 94.29) * mm, "end": v(53.12, 96.9) * mm});
            skLineSegment(sketch, "E397", {"start": v(53.12, 96.9) * mm, "end": v(52.93, 99.57) * mm});
            skLineSegment(sketch, "E398", {"start": v(52.93, 99.57) * mm, "end": v(49.44, 101.35) * mm});
            skLineSegment(sketch, "E399", {"start": v(49.44, 101.35) * mm, "end": v(47.18, 99.94) * mm});
            skLineSegment(sketch, "E400", {"start": v(47.18, 99.94) * mm, "end": v(45.02, 98.45) * mm});
            skLineSegment(sketch, "E401", {"start": v(45.02, 98.45) * mm, "end": v(42.98, 96.9) * mm});
            skLineSegment(sketch, "E402", {"start": v(42.98, 96.9) * mm, "end": v(41.06, 95.27) * mm});
            skLineSegment(sketch, "E403", {"start": v(41.06, 95.27) * mm, "end": v(39.28, 93.58) * mm});
            skLineSegment(sketch, "E404", {"start": v(39.28, 93.58) * mm, "end": v(37.65, 91.81) * mm});
            skLineSegment(sketch, "E405", {"start": v(37.65, 91.81) * mm, "end": v(36.18, 89.98) * mm});
            skLineSegment(sketch, "E406", {"start": v(36.18, 89.98) * mm, "end": v(34.73, 88.13) * mm});
            skLineSegment(sketch, "E407", {"start": v(34.73, 88.13) * mm, "end": v(33.28, 86.27) * mm});
            skLineSegment(sketch, "E408", {"start": v(33.28, 86.27) * mm, "end": v(27.88, 85.8) * mm});
            skLineSegment(sketch, "E409", {"start": v(27.88, 85.8) * mm, "end": v(23.78, 89.36) * mm});
            skLineSegment(sketch, "E410", {"start": v(23.78, 89.36) * mm, "end": v(23.7, 91.71) * mm});
            skLineSegment(sketch, "E411", {"start": v(23.7, 91.71) * mm, "end": v(23.62, 94.06) * mm});
            skLineSegment(sketch, "E412", {"start": v(23.62, 94.06) * mm, "end": v(23.5, 96.41) * mm});
            skLineSegment(sketch, "E413", {"start": v(23.5, 96.41) * mm, "end": v(23.22, 98.8) * mm});
            skLineSegment(sketch, "E414", {"start": v(23.22, 98.8) * mm, "end": v(22.78, 101.21) * mm});
            skLineSegment(sketch, "E415", {"start": v(22.78, 101.21) * mm, "end": v(22.18, 103.65) * mm});
            skLineSegment(sketch, "E416", {"start": v(22.18, 103.65) * mm, "end": v(21.45, 106.1) * mm});
            skLineSegment(sketch, "E417", {"start": v(21.45, 106.1) * mm, "end": v(20.58, 108.58) * mm});
            skLineSegment(sketch, "E418", {"start": v(20.58, 108.58) * mm, "end": v(19.57, 111.06) * mm});
            skLineSegment(sketch, "E419", {"start": v(19.57, 111.06) * mm, "end": v(15.7, 111.67) * mm});
            skLineSegment(sketch, "E420", {"start": v(15.7, 111.67) * mm, "end": v(15.7, 111.67) * mm});
            skCircle(sketch, "E421", {"center": v(0, 0) * mm, "radius": 125 * mm});
            skSolve(sketch);
        }
        {
            var Q0;
            Q0 = qSketchRegion(id + "F0", true);
            extrude(context, id + "F1", {"entities" : qUnion([Q0]), "depth" : 5 * mm});
        }
        {
            var Q0;
            Q0=makeQuery(id+"F1.opExtrude","CAP_FACE",FACE,{"disambiguationData":[OSD([sQuery(id+"F0.wireOp",EDGE,"E0"),sQuery(id+"F0.wireOp",EDGE,"E1"),sQuery(id+"F0.wireOp",EDGE,"E2"),sQuery(id+"F0.wireOp",EDGE,"E3"),sQuery(id+"F0.wireOp",EDGE,"E4"),sQuery(id+"F0.wireOp",EDGE,"E5"),sQuery(id+"F0.wireOp",EDGE,"E6"),sQuery(id+"F0.wireOp",EDGE,"E7"),sQuery(id+"F0.wireOp",EDGE,"E8"),sQuery(id+"F0.wireOp",EDGE,"E9"),sQuery(id+"F0.wireOp",EDGE,"E10"),sQuery(id+"F0.wireOp",EDGE,"E11"),sQuery(id+"F0.wireOp",EDGE,"E12"),sQuery(id+"F0.wireOp",EDGE,"E13"),sQuery(id+"F0.wireOp",EDGE,"E14"),sQuery(id+"F0.wireOp",EDGE,"E15"),sQuery(id+"F0.wireOp",EDGE,"E16"),sQuery(id+"F0.wireOp",EDGE,"E17"),sQuery(id+"F0.wireOp",EDGE,"E18"),sQuery(id+"F0.wireOp",EDGE,"E19"),sQuery(id+"F0.wireOp",EDGE,"E20"),sQuery(id+"F0.wireOp",EDGE,"E21"),sQuery(id+"F0.wireOp",EDGE,"E22"),sQuery(id+"F0.wireOp",EDGE,"E23"),sQuery(id+"F0.wireOp",EDGE,"E24"),sQuery(id+"F0.wireOp",EDGE,"E25"),sQuery(id+"F0.wireOp",EDGE,"E26"),sQuery(id+"F0.wireOp",EDGE,"E27"),sQuery(id+"F0.wireOp",EDGE,"E28"),sQuery(id+"F0.wireOp",EDGE,"E29"),sQuery(id+"F0.wireOp",EDGE,"E30"),sQuery(id+"F0.wireOp",EDGE,"E31"),sQuery(id+"F0.wireOp",EDGE,"E32"),sQuery(id+"F0.wireOp",EDGE,"E33"),sQuery(id+"F0.wireOp",EDGE,"E34"),sQuery(id+"F0.wireOp",EDGE,"E35"),sQuery(id+"F0.wireOp",EDGE,"E36"),sQuery(id+"F0.wireOp",EDGE,"E37"),sQuery(id+"F0.wireOp",EDGE,"E38"),sQuery(id+"F0.wireOp",EDGE,"E39"),sQuery(id+"F0.wireOp",EDGE,"E40"),sQuery(id+"F0.wireOp",EDGE,"E41"),sQuery(id+"F0.wireOp",EDGE,"E42"),sQuery(id+"F0.wireOp",EDGE,"E43"),sQuery(id+"F0.wireOp",EDGE,"E44"),sQuery(id+"F0.wireOp",EDGE,"E45"),sQuery(id+"F0.wireOp",EDGE,"E46"),sQuery(id+"F0.wireOp",EDGE,"E47"),sQuery(id+"F0.wireOp",EDGE,"E48"),sQuery(id+"F0.wireOp",EDGE,"E49"),sQuery(id+"F0.wireOp",EDGE,"E50"),sQuery(id+"F0.wireOp",EDGE,"E51"),sQuery(id+"F0.wireOp",EDGE,"E52"),sQuery(id+"F0.wireOp",EDGE,"E53"),sQuery(id+"F0.wireOp",EDGE,"E54"),sQuery(id+"F0.wireOp",EDGE,"E55"),sQuery(id+"F0.wireOp",EDGE,"E56"),sQuery(id+"F0.wireOp",EDGE,"E57"),sQuery(id+"F0.wireOp",EDGE,"E58"),sQuery(id+"F0.wireOp",EDGE,"E59"),sQuery(id+"F0.wireOp",EDGE,"E60"),sQuery(id+"F0.wireOp",EDGE,"E61"),sQuery(id+"F0.wireOp",EDGE,"E62"),sQuery(id+"F0.wireOp",EDGE,"E63"),sQuery(id+"F0.wireOp",EDGE,"E64"),sQuery(id+"F0.wireOp",EDGE,"E65"),sQuery(id+"F0.wireOp",EDGE,"E66"),sQuery(id+"F0.wireOp",EDGE,"E67"),sQuery(id+"F0.wireOp",EDGE,"E68"),sQuery(id+"F0.wireOp",EDGE,"E69"),sQuery(id+"F0.wireOp",EDGE,"E70"),sQuery(id+"F0.wireOp",EDGE,"E71"),sQuery(id+"F0.wireOp",EDGE,"E72"),sQuery(id+"F0.wireOp",EDGE,"E73"),sQuery(id+"F0.wireOp",EDGE,"E74"),sQuery(id+"F0.wireOp",EDGE,"E75"),sQuery(id+"F0.wireOp",EDGE,"E76"),sQuery(id+"F0.wireOp",EDGE,"E77"),sQuery(id+"F0.wireOp",EDGE,"E78"),sQuery(id+"F0.wireOp",EDGE,"E79"),sQuery(id+"F0.wireOp",EDGE,"E80"),sQuery(id+"F0.wireOp",EDGE,"E81"),sQuery(id+"F0.wireOp",EDGE,"E82"),sQuery(id+"F0.wireOp",EDGE,"E83"),sQuery(id+"F0.wireOp",EDGE,"E84"),sQuery(id+"F0.wireOp",EDGE,"E85"),sQuery(id+"F0.wireOp",EDGE,"E86"),sQuery(id+"F0.wireOp",EDGE,"E87"),sQuery(id+"F0.wireOp",EDGE,"E88"),sQuery(id+"F0.wireOp",EDGE,"E89"),sQuery(id+"F0.wireOp",EDGE,"E90"),sQuery(id+"F0.wireOp",EDGE,"E91"),sQuery(id+"F0.wireOp",EDGE,"E92"),sQuery(id+"F0.wireOp",EDGE,"E93"),sQuery(id+"F0.wireOp",EDGE,"E94"),sQuery(id+"F0.wireOp",EDGE,"E95"),sQuery(id+"F0.wireOp",EDGE,"E96"),sQuery(id+"F0.wireOp",EDGE,"E97"),sQuery(id+"F0.wireOp",EDGE,"E98"),sQuery(id+"F0.wireOp",EDGE,"E99"),sQuery(id+"F0.wireOp",EDGE,"E100"),sQuery(id+"F0.wireOp",EDGE,"E101"),sQuery(id+"F0.wireOp",EDGE,"E102"),sQuery(id+"F0.wireOp",EDGE,"E103"),sQuery(id+"F0.wireOp",EDGE,"E104"),sQuery(id+"F0.wireOp",EDGE,"E105"),sQuery(id+"F0.wireOp",EDGE,"E106"),sQuery(id+"F0.wireOp",EDGE,"E107"),sQuery(id+"F0.wireOp",EDGE,"E108"),sQuery(id+"F0.wireOp",EDGE,"E109"),sQuery(id+"F0.wireOp",EDGE,"E110"),sQuery(id+"F0.wireOp",EDGE,"E111"),sQuery(id+"F0.wireOp",EDGE,"E112"),sQuery(id+"F0.wireOp",EDGE,"E113"),sQuery(id+"F0.wireOp",EDGE,"E114"),sQuery(id+"F0.wireOp",EDGE,"E115"),sQuery(id+"F0.wireOp",EDGE,"E116"),sQuery(id+"F0.wireOp",EDGE,"E117"),sQuery(id+"F0.wireOp",EDGE,"E118"),sQuery(id+"F0.wireOp",EDGE,"E119"),sQuery(id+"F0.wireOp",EDGE,"E120"),sQuery(id+"F0.wireOp",EDGE,"E121"),sQuery(id+"F0.wireOp",EDGE,"E122"),sQuery(id+"F0.wireOp",EDGE,"E123"),sQuery(id+"F0.wireOp",EDGE,"E124"),sQuery(id+"F0.wireOp",EDGE,"E125"),sQuery(id+"F0.wireOp",EDGE,"E126"),sQuery(id+"F0.wireOp",EDGE,"E127"),sQuery(id+"F0.wireOp",EDGE,"E128"),sQuery(id+"F0.wireOp",EDGE,"E129"),sQuery(id+"F0.wireOp",EDGE,"E130"),sQuery(id+"F0.wireOp",EDGE,"E131"),sQuery(id+"F0.wireOp",EDGE,"E132"),sQuery(id+"F0.wireOp",EDGE,"E133"),sQuery(id+"F0.wireOp",EDGE,"E134"),sQuery(id+"F0.wireOp",EDGE,"E135"),sQuery(id+"F0.wireOp",EDGE,"E136"),sQuery(id+"F0.wireOp",EDGE,"E137"),sQuery(id+"F0.wireOp",EDGE,"E138"),sQuery(id+"F0.wireOp",EDGE,"E139"),sQuery(id+"F0.wireOp",EDGE,"E140"),sQuery(id+"F0.wireOp",EDGE,"E141"),sQuery(id+"F0.wireOp",EDGE,"E142"),sQuery(id+"F0.wireOp",EDGE,"E143"),sQuery(id+"F0.wireOp",EDGE,"E144"),sQuery(id+"F0.wireOp",EDGE,"E145"),sQuery(id+"F0.wireOp",EDGE,"E146"),sQuery(id+"F0.wireOp",EDGE,"E147"),sQuery(id+"F0.wireOp",EDGE,"E148"),sQuery(id+"F0.wireOp",EDGE,"E149"),sQuery(id+"F0.wireOp",EDGE,"E150"),sQuery(id+"F0.wireOp",EDGE,"E151"),sQuery(id+"F0.wireOp",EDGE,"E152"),sQuery(id+"F0.wireOp",EDGE,"E153"),sQuery(id+"F0.wireOp",EDGE,"E154"),sQuery(id+"F0.wireOp",EDGE,"E155"),sQuery(id+"F0.wireOp",EDGE,"E156"),sQuery(id+"F0.wireOp",EDGE,"E157"),sQuery(id+"F0.wireOp",EDGE,"E158"),sQuery(id+"F0.wireOp",EDGE,"E159"),sQuery(id+"F0.wireOp",EDGE,"E160"),sQuery(id+"F0.wireOp",EDGE,"E161"),sQuery(id+"F0.wireOp",EDGE,"E162"),sQuery(id+"F0.wireOp",EDGE,"E163"),sQuery(id+"F0.wireOp",EDGE,"E164"),sQuery(id+"F0.wireOp",EDGE,"E165"),sQuery(id+"F0.wireOp",EDGE,"E166"),sQuery(id+"F0.wireOp",EDGE,"E167"),sQuery(id+"F0.wireOp",EDGE,"E168"),sQuery(id+"F0.wireOp",EDGE,"E169"),sQuery(id+"F0.wireOp",EDGE,"E170"),sQuery(id+"F0.wireOp",EDGE,"E171"),sQuery(id+"F0.wireOp",EDGE,"E172"),sQuery(id+"F0.wireOp",EDGE,"E173"),sQuery(id+"F0.wireOp",EDGE,"E174"),sQuery(id+"F0.wireOp",EDGE,"E175"),sQuery(id+"F0.wireOp",EDGE,"E176"),sQuery(id+"F0.wireOp",EDGE,"E177"),sQuery(id+"F0.wireOp",EDGE,"E178"),sQuery(id+"F0.wireOp",EDGE,"E179"),sQuery(id+"F0.wireOp",EDGE,"E180"),sQuery(id+"F0.wireOp",EDGE,"E181"),sQuery(id+"F0.wireOp",EDGE,"E182"),sQuery(id+"F0.wireOp",EDGE,"E183"),sQuery(id+"F0.wireOp",EDGE,"E184"),sQuery(id+"F0.wireOp",EDGE,"E185"),sQuery(id+"F0.wireOp",EDGE,"E186"),sQuery(id+"F0.wireOp",EDGE,"E187"),sQuery(id+"F0.wireOp",EDGE,"E188"),sQuery(id+"F0.wireOp",EDGE,"E189"),sQuery(id+"F0.wireOp",EDGE,"E190"),sQuery(id+"F0.wireOp",EDGE,"E191"),sQuery(id+"F0.wireOp",EDGE,"E192"),sQuery(id+"F0.wireOp",EDGE,"E193"),sQuery(id+"F0.wireOp",EDGE,"E194"),sQuery(id+"F0.wireOp",EDGE,"E195"),sQuery(id+"F0.wireOp",EDGE,"E196"),sQuery(id+"F0.wireOp",EDGE,"E197"),sQuery(id+"F0.wireOp",EDGE,"E198"),sQuery(id+"F0.wireOp",EDGE,"E199"),sQuery(id+"F0.wireOp",EDGE,"E200"),sQuery(id+"F0.wireOp",EDGE,"E201"),sQuery(id+"F0.wireOp",EDGE,"E202"),sQuery(id+"F0.wireOp",EDGE,"E203"),sQuery(id+"F0.wireOp",EDGE,"E204"),sQuery(id+"F0.wireOp",EDGE,"E205"),sQuery(id+"F0.wireOp",EDGE,"E206"),sQuery(id+"F0.wireOp",EDGE,"E207"),sQuery(id+"F0.wireOp",EDGE,"E208"),sQuery(id+"F0.wireOp",EDGE,"E209"),sQuery(id+"F0.wireOp",EDGE,"E210"),sQuery(id+"F0.wireOp",EDGE,"E211"),sQuery(id+"F0.wireOp",EDGE,"E212"),sQuery(id+"F0.wireOp",EDGE,"E213"),sQuery(id+"F0.wireOp",EDGE,"E214"),sQuery(id+"F0.wireOp",EDGE,"E215"),sQuery(id+"F0.wireOp",EDGE,"E216"),sQuery(id+"F0.wireOp",EDGE,"E217"),sQuery(id+"F0.wireOp",EDGE,"E218"),sQuery(id+"F0.wireOp",EDGE,"E219"),sQuery(id+"F0.wireOp",EDGE,"E220"),sQuery(id+"F0.wireOp",EDGE,"E221"),sQuery(id+"F0.wireOp",EDGE,"E222"),sQuery(id+"F0.wireOp",EDGE,"E223"),sQuery(id+"F0.wireOp",EDGE,"E224"),sQuery(id+"F0.wireOp",EDGE,"E225"),sQuery(id+"F0.wireOp",EDGE,"E226"),sQuery(id+"F0.wireOp",EDGE,"E227"),sQuery(id+"F0.wireOp",EDGE,"E228"),sQuery(id+"F0.wireOp",EDGE,"E229"),sQuery(id+"F0.wireOp",EDGE,"E230"),sQuery(id+"F0.wireOp",EDGE,"E231"),sQuery(id+"F0.wireOp",EDGE,"E232"),sQuery(id+"F0.wireOp",EDGE,"E233"),sQuery(id+"F0.wireOp",EDGE,"E234"),sQuery(id+"F0.wireOp",EDGE,"E235"),sQuery(id+"F0.wireOp",EDGE,"E236"),sQuery(id+"F0.wireOp",EDGE,"E237"),sQuery(id+"F0.wireOp",EDGE,"E238"),sQuery(id+"F0.wireOp",EDGE,"E239"),sQuery(id+"F0.wireOp",EDGE,"E240"),sQuery(id+"F0.wireOp",EDGE,"E241"),sQuery(id+"F0.wireOp",EDGE,"E242"),sQuery(id+"F0.wireOp",EDGE,"E243"),sQuery(id+"F0.wireOp",EDGE,"E244"),sQuery(id+"F0.wireOp",EDGE,"E245"),sQuery(id+"F0.wireOp",EDGE,"E246"),sQuery(id+"F0.wireOp",EDGE,"E247"),sQuery(id+"F0.wireOp",EDGE,"E248"),sQuery(id+"F0.wireOp",EDGE,"E249"),sQuery(id+"F0.wireOp",EDGE,"E250"),sQuery(id+"F0.wireOp",EDGE,"E251"),sQuery(id+"F0.wireOp",EDGE,"E252"),sQuery(id+"F0.wireOp",EDGE,"E253"),sQuery(id+"F0.wireOp",EDGE,"E254"),sQuery(id+"F0.wireOp",EDGE,"E255"),sQuery(id+"F0.wireOp",EDGE,"E256"),sQuery(id+"F0.wireOp",EDGE,"E257"),sQuery(id+"F0.wireOp",EDGE,"E258"),sQuery(id+"F0.wireOp",EDGE,"E259"),sQuery(id+"F0.wireOp",EDGE,"E260"),sQuery(id+"F0.wireOp",EDGE,"E261"),sQuery(id+"F0.wireOp",EDGE,"E262"),sQuery(id+"F0.wireOp",EDGE,"E263"),sQuery(id+"F0.wireOp",EDGE,"E264"),sQuery(id+"F0.wireOp",EDGE,"E265"),sQuery(id+"F0.wireOp",EDGE,"E266"),sQuery(id+"F0.wireOp",EDGE,"E267"),sQuery(id+"F0.wireOp",EDGE,"E268"),sQuery(id+"F0.wireOp",EDGE,"E269"),sQuery(id+"F0.wireOp",EDGE,"E270"),sQuery(id+"F0.wireOp",EDGE,"E271"),sQuery(id+"F0.wireOp",EDGE,"E272"),sQuery(id+"F0.wireOp",EDGE,"E273"),sQuery(id+"F0.wireOp",EDGE,"E274"),sQuery(id+"F0.wireOp",EDGE,"E275"),sQuery(id+"F0.wireOp",EDGE,"E276"),sQuery(id+"F0.wireOp",EDGE,"E277"),sQuery(id+"F0.wireOp",EDGE,"E278"),sQuery(id+"F0.wireOp",EDGE,"E279"),sQuery(id+"F0.wireOp",EDGE,"E280"),sQuery(id+"F0.wireOp",EDGE,"E281"),sQuery(id+"F0.wireOp",EDGE,"E282"),sQuery(id+"F0.wireOp",EDGE,"E283"),sQuery(id+"F0.wireOp",EDGE,"E284"),sQuery(id+"F0.wireOp",EDGE,"E285"),sQuery(id+"F0.wireOp",EDGE,"E286"),sQuery(id+"F0.wireOp",EDGE,"E287"),sQuery(id+"F0.wireOp",EDGE,"E288"),sQuery(id+"F0.wireOp",EDGE,"E289"),sQuery(id+"F0.wireOp",EDGE,"E290"),sQuery(id+"F0.wireOp",EDGE,"E291"),sQuery(id+"F0.wireOp",EDGE,"E292"),sQuery(id+"F0.wireOp",EDGE,"E293"),sQuery(id+"F0.wireOp",EDGE,"E294"),sQuery(id+"F0.wireOp",EDGE,"E295"),sQuery(id+"F0.wireOp",EDGE,"E296"),sQuery(id+"F0.wireOp",EDGE,"E297"),sQuery(id+"F0.wireOp",EDGE,"E298"),sQuery(id+"F0.wireOp",EDGE,"E299"),sQuery(id+"F0.wireOp",EDGE,"E300"),sQuery(id+"F0.wireOp",EDGE,"E301"),sQuery(id+"F0.wireOp",EDGE,"E302"),sQuery(id+"F0.wireOp",EDGE,"E303"),sQuery(id+"F0.wireOp",EDGE,"E304"),sQuery(id+"F0.wireOp",EDGE,"E305"),sQuery(id+"F0.wireOp",EDGE,"E306"),sQuery(id+"F0.wireOp",EDGE,"E307"),sQuery(id+"F0.wireOp",EDGE,"E308"),sQuery(id+"F0.wireOp",EDGE,"E309"),sQuery(id+"F0.wireOp",EDGE,"E310"),sQuery(id+"F0.wireOp",EDGE,"E311"),sQuery(id+"F0.wireOp",EDGE,"E312"),sQuery(id+"F0.wireOp",EDGE,"E313"),sQuery(id+"F0.wireOp",EDGE,"E314"),sQuery(id+"F0.wireOp",EDGE,"E315"),sQuery(id+"F0.wireOp",EDGE,"E316"),sQuery(id+"F0.wireOp",EDGE,"E317"),sQuery(id+"F0.wireOp",EDGE,"E318"),sQuery(id+"F0.wireOp",EDGE,"E319"),sQuery(id+"F0.wireOp",EDGE,"E320"),sQuery(id+"F0.wireOp",EDGE,"E321"),sQuery(id+"F0.wireOp",EDGE,"E322"),sQuery(id+"F0.wireOp",EDGE,"E323"),sQuery(id+"F0.wireOp",EDGE,"E324"),sQuery(id+"F0.wireOp",EDGE,"E325"),sQuery(id+"F0.wireOp",EDGE,"E326"),sQuery(id+"F0.wireOp",EDGE,"E327"),sQuery(id+"F0.wireOp",EDGE,"E328"),sQuery(id+"F0.wireOp",EDGE,"E329"),sQuery(id+"F0.wireOp",EDGE,"E330"),sQuery(id+"F0.wireOp",EDGE,"E331"),sQuery(id+"F0.wireOp",EDGE,"E332"),sQuery(id+"F0.wireOp",EDGE,"E333"),sQuery(id+"F0.wireOp",EDGE,"E334"),sQuery(id+"F0.wireOp",EDGE,"E335"),sQuery(id+"F0.wireOp",EDGE,"E336"),sQuery(id+"F0.wireOp",EDGE,"E337"),sQuery(id+"F0.wireOp",EDGE,"E338"),sQuery(id+"F0.wireOp",EDGE,"E339"),sQuery(id+"F0.wireOp",EDGE,"E340"),sQuery(id+"F0.wireOp",EDGE,"E341"),sQuery(id+"F0.wireOp",EDGE,"E342"),sQuery(id+"F0.wireOp",EDGE,"E343"),sQuery(id+"F0.wireOp",EDGE,"E344"),sQuery(id+"F0.wireOp",EDGE,"E345"),sQuery(id+"F0.wireOp",EDGE,"E346"),sQuery(id+"F0.wireOp",EDGE,"E347"),sQuery(id+"F0.wireOp",EDGE,"E348"),sQuery(id+"F0.wireOp",EDGE,"E349"),sQuery(id+"F0.wireOp",EDGE,"E350"),sQuery(id+"F0.wireOp",EDGE,"E351"),sQuery(id+"F0.wireOp",EDGE,"E352"),sQuery(id+"F0.wireOp",EDGE,"E353"),sQuery(id+"F0.wireOp",EDGE,"E354"),sQuery(id+"F0.wireOp",EDGE,"E355"),sQuery(id+"F0.wireOp",EDGE,"E356"),sQuery(id+"F0.wireOp",EDGE,"E357"),sQuery(id+"F0.wireOp",EDGE,"E358"),sQuery(id+"F0.wireOp",EDGE,"E359"),sQuery(id+"F0.wireOp",EDGE,"E360"),sQuery(id+"F0.wireOp",EDGE,"E361"),sQuery(id+"F0.wireOp",EDGE,"E362"),sQuery(id+"F0.wireOp",EDGE,"E363"),sQuery(id+"F0.wireOp",EDGE,"E364"),sQuery(id+"F0.wireOp",EDGE,"E365"),sQuery(id+"F0.wireOp",EDGE,"E366"),sQuery(id+"F0.wireOp",EDGE,"E367"),sQuery(id+"F0.wireOp",EDGE,"E368"),sQuery(id+"F0.wireOp",EDGE,"E369"),sQuery(id+"F0.wireOp",EDGE,"E370"),sQuery(id+"F0.wireOp",EDGE,"E371"),sQuery(id+"F0.wireOp",EDGE,"E372"),sQuery(id+"F0.wireOp",EDGE,"E373"),sQuery(id+"F0.wireOp",EDGE,"E374"),sQuery(id+"F0.wireOp",EDGE,"E375"),sQuery(id+"F0.wireOp",EDGE,"E376"),sQuery(id+"F0.wireOp",EDGE,"E377"),sQuery(id+"F0.wireOp",EDGE,"E378"),sQuery(id+"F0.wireOp",EDGE,"E379"),sQuery(id+"F0.wireOp",EDGE,"E380"),sQuery(id+"F0.wireOp",EDGE,"E381"),sQuery(id+"F0.wireOp",EDGE,"E382"),sQuery(id+"F0.wireOp",EDGE,"E383"),sQuery(id+"F0.wireOp",EDGE,"E384"),sQuery(id+"F0.wireOp",EDGE,"E385"),sQuery(id+"F0.wireOp",EDGE,"E386"),sQuery(id+"F0.wireOp",EDGE,"E387"),sQuery(id+"F0.wireOp",EDGE,"E388"),sQuery(id+"F0.wireOp",EDGE,"E389"),sQuery(id+"F0.wireOp",EDGE,"E390"),sQuery(id+"F0.wireOp",EDGE,"E391"),sQuery(id+"F0.wireOp",EDGE,"E392"),sQuery(id+"F0.wireOp",EDGE,"E393"),sQuery(id+"F0.wireOp",EDGE,"E394"),sQuery(id+"F0.wireOp",EDGE,"E395"),sQuery(id+"F0.wireOp",EDGE,"E396"),sQuery(id+"F0.wireOp",EDGE,"E397"),sQuery(id+"F0.wireOp",EDGE,"E398"),sQuery(id+"F0.wireOp",EDGE,"E399"),sQuery(id+"F0.wireOp",EDGE,"E400"),sQuery(id+"F0.wireOp",EDGE,"E401"),sQuery(id+"F0.wireOp",EDGE,"E402"),sQuery(id+"F0.wireOp",EDGE,"E403"),sQuery(id+"F0.wireOp",EDGE,"E404"),sQuery(id+"F0.wireOp",EDGE,"E405"),sQuery(id+"F0.wireOp",EDGE,"E406"),sQuery(id+"F0.wireOp",EDGE,"E407"),sQuery(id+"F0.wireOp",EDGE,"E408"),sQuery(id+"F0.wireOp",EDGE,"E409"),sQuery(id+"F0.wireOp",EDGE,"E410"),sQuery(id+"F0.wireOp",EDGE,"E411"),sQuery(id+"F0.wireOp",EDGE,"E412"),sQuery(id+"F0.wireOp",EDGE,"E413"),sQuery(id+"F0.wireOp",EDGE,"E414"),sQuery(id+"F0.wireOp",EDGE,"E415"),sQuery(id+"F0.wireOp",EDGE,"E416"),sQuery(id+"F0.wireOp",EDGE,"E417"),sQuery(id+"F0.wireOp",EDGE,"E418"),sQuery(id+"F0.wireOp",EDGE,"E419"),sQuery(id+"F0.wireOp",EDGE,"E421")])],"isStart":true});
            var sketch = newSketch(context, id + "F2", { "sketchPlane" : qUnion([Q0])});
            skCircle(sketch, "E422", {"center": v(0, 0) * mm, "radius": 125 * mm});
            skSolve(sketch);
        }
        {
            var Q0;
            Q0=makeQuery(id+"F2.imprint","IMPRINT",FACE,{"disambiguationData":[TD([[makeQuery(id+"F2.imprint","IMPRINT",EDGE,{"derivedFrom":sQuery(id+"F2.wireOp",EDGE,"E422")}),-1.0]])]});
            var Q1;
            Q1=makeQuery(id+"F2.imprint","IMPRINT",FACE,{"disambiguationData":[TD([[makeQuery(id+"F2.imprint","IMPRINT",EDGE,{"derivedFrom":makeQuery(id+"F1.opExtrude","CAP_EDGE",EDGE,{"disambiguationData":[OSD([sQuery(id+"F0.wireOp",EDGE,"E0")])],"isStart":true})}),-1.0]])]});
            extrude(context, id + "F3", {"entities" : qUnion([Q0, Q1]), "operationType" : NewBodyOperationType.ADD, "depth" : 5 * mm});
        }
        {
            var Q0;
            Q0=makeQuery(id+"F3.opExtrude","CAP_FACE",FACE,{"disambiguationData":[OSD([sQuery(id+"F2.wireOp",EDGE,"E422")])],"isStart":false});
            var sketch = newSketch(context, id + "F4", { "sketchPlane" : qUnion([Q0])});
            skCircle(sketch, "E423", {"center": v(0, 0) * mm, "radius": 5 * mm});
            skSolve(sketch);
        }
        {
            var Q0;
            Q0 = qSketchRegion(id + "F4", true);
            extrude(context, id + "F5", {"entities" : qUnion([Q0]), "operationType" : NewBodyOperationType.REMOVE, "endBound" : BoundingType.THROUGH_ALL, "oppositeDirection" : true, "depth" : 25 * mm});
        }
        {
            var Q0;
            Q0=makeQuery(id+"F3.opExtrude","CAP_FACE",FACE,{"disambiguationData":[OSD([sQuery(id+"F2.wireOp",EDGE,"E422")])],"isStart":true});
            var sketch = newSketch(context, id + "F6", { "sketchPlane" : qUnion([Q0])});
            skCircle(sketch, "E424", {"center": v(50, 0) * mm, "radius": 30 * mm});
            skCircle(sketch, "E425.1.0", {"center": v(0, 50) * mm, "radius": 30 * mm});
            skCircle(sketch, "E425.2.0", {"center": v(-50, 0) * mm, "radius": 30 * mm});
            skCircle(sketch, "E425.3.0", {"center": v(0, -50) * mm, "radius": 30 * mm});
            skPoint(sketch, "E425.center", {"position": v(0, 0) * mm});
            skSolve(sketch);
        }
        {
            var Q0;
            Q0 = qSketchRegion(id + "F6", true);
            extrude(context, id + "F7", {"entities" : qUnion([Q0]), "operationType" : NewBodyOperationType.REMOVE, "endBound" : BoundingType.THROUGH_ALL, "oppositeDirection" : true, "depth" : 25 * mm});
        }
        {
            var Q0;
            Q0=makeQuery(id+"F3.opExtrude","CAP_FACE",FACE,{"disambiguationData":[OSD([sQuery(id+"F2.wireOp",EDGE,"E422")])],"isStart":false});
            var sketch = newSketch(context, id + "F8", { "sketchPlane" : qUnion([Q0])});
            skCircle(sketch, "E426", {"center": v(-50.12, -48.87) * mm, "radius": 12.5 * mm});
            skCircle(sketch, "E427.1.0", {"center": v(48.87, -50.12) * mm, "radius": 12.5 * mm});
            skCircle(sketch, "E427.2.0", {"center": v(50.12, 48.87) * mm, "radius": 12.5 * mm});
            skCircle(sketch, "E427.3.0", {"center": v(-48.87, 50.12) * mm, "radius": 12.5 * mm});
            skPoint(sketch, "E427.center", {"position": v(0, 0) * mm});
            skSolve(sketch);
        }
        {
            var Q0;
            Q0 = qSketchRegion(id + "F8", true);
            extrude(context, id + "F9", {"entities" : qUnion([Q0]), "operationType" : NewBodyOperationType.REMOVE, "endBound" : BoundingType.THROUGH_ALL, "oppositeDirection" : true, "depth" : 25 * mm});
        }
    });
